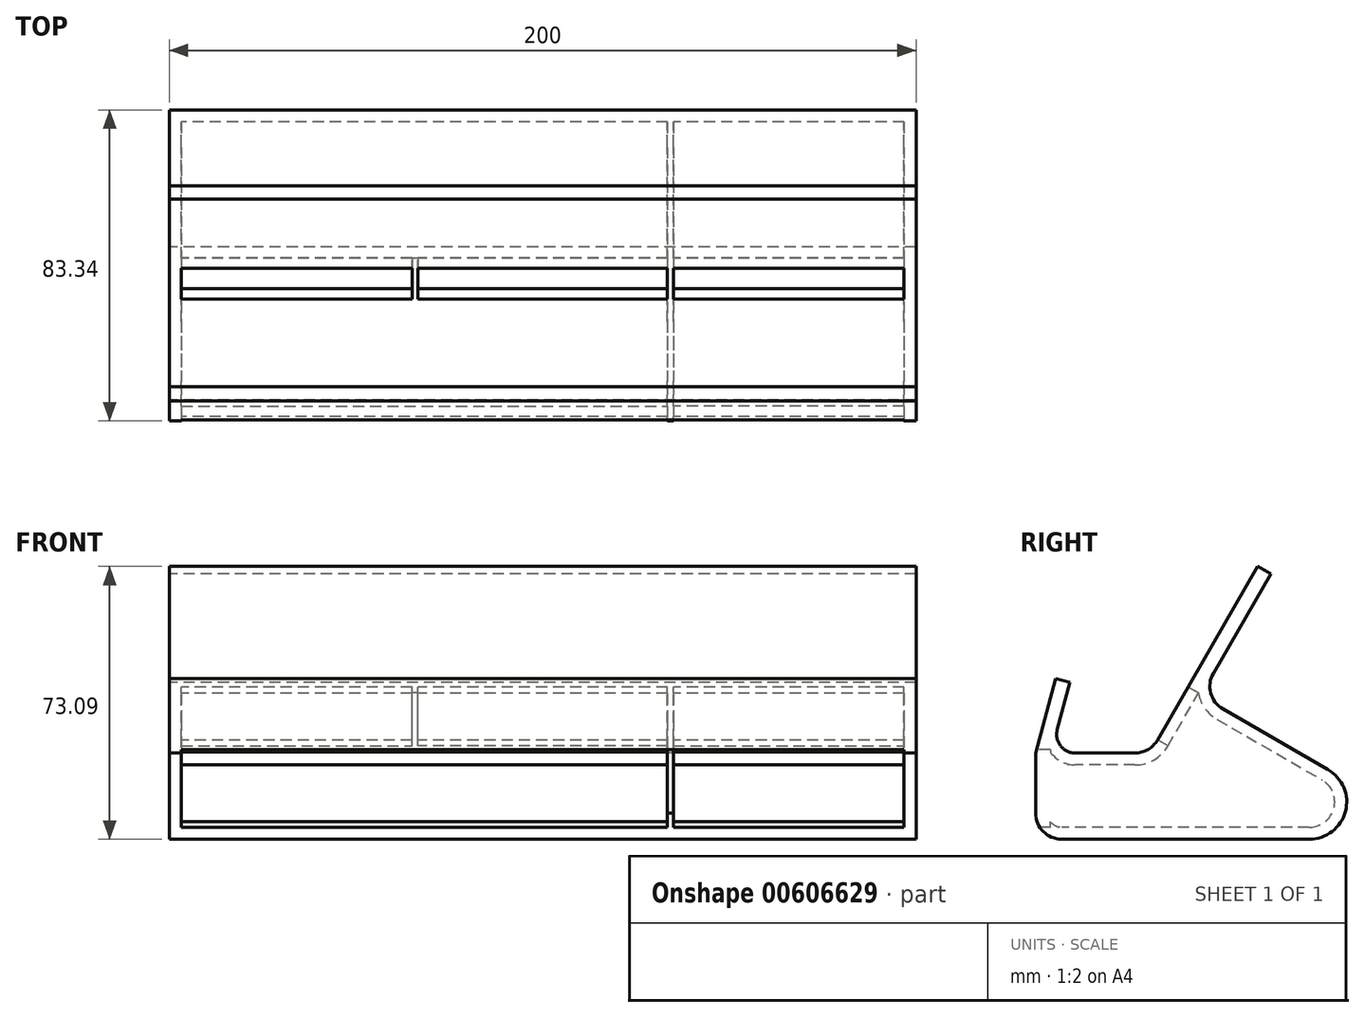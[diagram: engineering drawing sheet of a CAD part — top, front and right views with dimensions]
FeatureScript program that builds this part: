
annotation { "Feature Type Name" : "Feature", "Feature Type Description" : "" }
export const myFeature = defineFeature(function(context is Context, id is Id, definition is map)
    precondition{}
    {
        {
            var Q0;
            Q0=qCreatedBy(makeId("Right.planeOp"),FACE);
            var sketch = newSketch(context, id + "F0", { "sketchPlane" : qUnion([Q0])});
            skLineSegment(sketch, "E0.0", {"start": v(-47.73, -25.37) * mm, "end": v(-44.33, -12.7) * mm});
            skLineSegment(sketch, "E0.1", {"start": v(-22.9, -31.66) * mm, "end": v(-42.9, -31.66) * mm});
            skLineSegment(sketch, "E0.5", {"start": v(-22.9, -31.66) * mm, "end": v(5.97, 18.34) * mm});
            skLineSegment(sketch, "E1.0", {"start": v(-53.56, -31.66) * mm, "end": v(-48.2, -11.66) * mm});
            skLineSegment(sketch, "E2.1", {"start": v(-9.43, -16.34) * mm, "end": v(9.43, 16.34) * mm});
            skLineSegment(sketch, "E3", {"start": v(-48.2, -11.66) * mm, "end": v(-44.33, -12.7) * mm});
            skLineSegment(sketch, "E4", {"start": v(5.97, 18.34) * mm, "end": v(9.43, 16.34) * mm});
            skPoint(sketch, "E5", {"position": v(0, 0) * mm});
            skLineSegment(sketch, "E6", {"start": v(-9.43, -16.34) * mm, "end": v(57.1, -54.75) * mm});
            skLineSegment(sketch, "E7", {"start": v(57.1, -54.75) * mm, "end": v(-53.56, -54.75) * mm});
            skLineSegment(sketch, "E8", {"start": v(-53.56, -54.75) * mm, "end": v(-53.56, -31.66) * mm});
            skLineSegment(sketch, "E9", {"start": v(-9.43, -16.34) * mm, "end": v(-12.9, -14.34) * mm, "construction": true});
            skArc(sketch, "E10", {"start": v(-47.73, -25.37) * mm, "mid": v(-46.86, -29.7) * mm, "end": v(-42.9, -31.66) * mm});
            skSolve(sketch);
        }
        {
            var Q0;
            Q0=qSketchRegion(id+"F0",true);
            extrude(context, id + "F1", {"entities" : qUnion([Q0]), "endBound" : BoundingType.SYMMETRIC, "depth" : 200 * mm, "offsetDistance" : 25 * mm});
        }
        {
            var Q0;
            Q0=makeQuery(id+"F1.opExtrude","SWEPT_EDGE",EDGE,{"disambiguationData":[OSD([sQuery(id+"F0.wireOp",EDGE,"E7"),sQuery(id+"F0.wireOp",EDGE,"E8")])]});
            var Q1;
            Q1=makeQuery(id+"F1.opExtrude","SWEPT_EDGE",EDGE,{"disambiguationData":[OSD([sQuery(id+"F0.wireOp",EDGE,"E2.1"),sQuery(id+"F0.wireOp",EDGE,"E6")])]});
            var Q2;
            Q2=makeQuery(id+"F1.opExtrude","SWEPT_EDGE",EDGE,{"disambiguationData":[OSD([sQuery(id+"F0.wireOp",EDGE,"E0.1"),sQuery(id+"F0.wireOp",EDGE,"E0.5")])]});
            fillet(context, id + "F2", {"entities" : qUnion([Q0, Q1, Q2]), "radius" : 7 * mm, "tangentPropagation" : true, "allowEdgeOverflow" : false});
        }
        {
            var Q0;
            Q0=makeQuery(id+"F1.opExtrude","SWEPT_EDGE",EDGE,{"disambiguationData":[OSD([sQuery(id+"F0.wireOp",EDGE,"E6"),sQuery(id+"F0.wireOp",EDGE,"E7")])]});
            fillet(context, id + "F3", {"entities" : qUnion([Q0]), "radius" : 10 * mm, "tangentPropagation" : true, "allowEdgeOverflow" : false});
        }
        {
            var Q0;
            Q0=makeQuery(id+"F1.opExtrude","SWEPT_FACE",FACE,{"disambiguationData":[OSD([sQuery(id+"F0.wireOp",EDGE,"E8")])]});
            var Q1;
            Q1=makeQuery(id+"F1.opExtrude","SWEPT_BODY",BODY,{"disambiguationData":[OSD([sQuery(id+"F0.wireOp",EDGE,"E0.0"),sQuery(id+"F0.wireOp",EDGE,"E0.1"),sQuery(id+"F0.wireOp",EDGE,"E0.5"),sQuery(id+"F0.wireOp",EDGE,"E1.0"),sQuery(id+"F0.wireOp",EDGE,"E2.1"),sQuery(id+"F0.wireOp",EDGE,"E3"),sQuery(id+"F0.wireOp",EDGE,"E4"),sQuery(id+"F0.wireOp",EDGE,"E6"),sQuery(id+"F0.wireOp",EDGE,"E7"),sQuery(id+"F0.wireOp",EDGE,"E8"),sQuery(id+"F0.wireOp",EDGE,"E10")])]});
            shell(context, id + "F4", {"isHollow" : true, "entities" : qUnion([Q0]), "parts" : qUnion([Q1]), "thickness" : 3.2 * mm});
        }
        {
            var Q0;
            Q0=makeQuery(id+"F1.opExtrude","SWEPT_FACE",FACE,{"disambiguationData":[OSD([sQuery(id+"F0.wireOp",EDGE,"E8")])]});
            var sketch = newSketch(context, id + "F5", { "sketchPlane" : qUnion([Q0])});
            skLineSegment(sketch, "E11.bottom", {"start": v(-96.8, -30.76) * mm, "end": v(96.8, -30.76) * mm});
            skLineSegment(sketch, "E11.left", {"start": v(-96.8, -30.76) * mm, "end": v(-96.8, -51.55) * mm});
            skLineSegment(sketch, "E11.right", {"start": v(96.8, -30.76) * mm, "end": v(96.8, -51.55) * mm});
            skLineSegment(sketch, "E12", {"start": v(96.8, -51.55) * mm, "end": v(-96.8, -51.55) * mm});
            skSolve(sketch);
        }
        {
            var Q0;
            Q0 = qSketchRegion(id + "F5", true);
            extrude(context, id + "F6", {"entities" : qUnion([Q0]), "operationType" : NewBodyOperationType.REMOVE, "oppositeDirection" : true, "depth" : 4 * mm, "offsetDistance" : 25 * mm});
        }
        {
            var Q0;
            Q0=qCreatedBy(makeId("Right.planeOp"),FACE);
            cPlane(context, id + "F7", {"entities" : qUnion([Q0]), "cplaneType" : CPlaneType.OFFSET, "offset" : 35 * mm, "width" : 150 * mm, "height" : 150 * mm});
        }
        {
            var Q0;
            Q0=qCreatedBy(id+"F7.planeOp",FACE);
            var sketch = newSketch(context, id + "F8", { "sketchPlane" : qUnion([Q0])});
            skLineSegment(sketch, "E13.0", {"start": v(-49.56, -30.76) * mm, "end": v(-53.31, -30.76) * mm});
            skLineSegment(sketch, "E14.0", {"start": v(-49.56, -30.76) * mm, "end": v(-49.56, -31.45) * mm});
            skLineSegment(sketch, "E15.0", {"start": v(-49.56, -30.76) * mm, "end": v(-49.56, -30.76) * mm});
            skArc(sketch, "E16.0", {"start": v(-49.56, -31.45) * mm, "mid": v(-46.64, -33.96) * mm, "end": v(-42.9, -34.86) * mm});
            skLineSegment(sketch, "E17.0", {"start": v(-26.94, -34.86) * mm, "end": v(-42.9, -34.86) * mm});
            skLineSegment(sketch, "E18.0", {"start": v(-18.1, -29.76) * mm, "end": v(-9.91, -15.57) * mm});
            skArc(sketch, "E19.0", {"start": v(-18.1, -29.76) * mm, "mid": v(-21.84, -33.5) * mm, "end": v(-26.94, -34.86) * mm});
            skArc(sketch, "E20.0", {"start": v(-4.97, -22.61) * mm, "mid": v(-8.22, -19.64) * mm, "end": v(-9.91, -15.57) * mm});
            skLineSegment(sketch, "E21.0", {"start": v(-4.97, -22.61) * mm, "end": v(23.18, -38.87) * mm});
            skArc(sketch, "E22.0", {"start": v(19.78, -51.55) * mm, "mid": v(26.35, -46.51) * mm, "end": v(23.18, -38.87) * mm});
            skLineSegment(sketch, "E23.0", {"start": v(19.78, -51.55) * mm, "end": v(-46.56, -51.55) * mm});
            skLineSegment(sketch, "E24.0", {"start": v(-46.56, -51.55) * mm, "end": v(-52.43, -51.55) * mm});
            skLineSegment(sketch, "E25.0", {"start": v(-46.56, -51.55) * mm, "end": v(-46.56, -51.55) * mm});
            skLineSegment(sketch, "E26", {"start": v(-53.31, -30.76) * mm, "end": v(-53.56, -47.75) * mm});
            skArc(sketch, "E27", {"start": v(-53.56, -47.75) * mm, "mid": v(-53.27, -49.74) * mm, "end": v(-52.43, -51.55) * mm});
            skSolve(sketch);
        }
        {
            var Q0;
            Q0 = qSketchRegion(id + "F8", true);
            extrude(context, id + "F9", {"entities" : qUnion([Q0]), "operationType" : NewBodyOperationType.ADD, "oppositeDirection" : true, "depth" : 1.6 * mm, "offsetDistance" : 25 * mm});
        }
        {
            var Q0;
            Q0=makeQuery(id+"F1.opExtrude","SWEPT_FACE",FACE,{"disambiguationData":[OSD([sQuery(id+"F0.wireOp",EDGE,"E0.5")])]});
            var sketch = newSketch(context, id + "F10", { "sketchPlane" : qUnion([Q0])});
            skLineSegment(sketch, "E28.bottom", {"start": v(-35, -34.83) * mm, "end": v(-96.8, -34.83) * mm});
            skLineSegment(sketch, "E28.top", {"start": v(-35, -18.44) * mm, "end": v(-96.8, -18.44) * mm});
            skLineSegment(sketch, "E28.left", {"start": v(-35, -34.83) * mm, "end": v(-35, -18.44) * mm});
            skLineSegment(sketch, "E28.right", {"start": v(-96.8, -34.83) * mm, "end": v(-96.8, -18.44) * mm});
            skLineSegment(sketch, "E29.bottom", {"start": v(33.4, -34.83) * mm, "end": v(-33.4, -34.83) * mm});
            skLineSegment(sketch, "E29.top", {"start": v(33.4, -18.44) * mm, "end": v(-33.4, -18.44) * mm});
            skLineSegment(sketch, "E29.left", {"start": v(33.4, -34.83) * mm, "end": v(33.4, -18.44) * mm});
            skLineSegment(sketch, "E29.right", {"start": v(-33.4, -34.83) * mm, "end": v(-33.4, -18.44) * mm});
            skLineSegment(sketch, "E30.bottom", {"start": v(96.8, -34.83) * mm, "end": v(35, -34.83) * mm});
            skLineSegment(sketch, "E30.top", {"start": v(96.8, -18.44) * mm, "end": v(35, -18.44) * mm});
            skLineSegment(sketch, "E30.left", {"start": v(96.8, -34.83) * mm, "end": v(96.8, -18.44) * mm});
            skLineSegment(sketch, "E30.right", {"start": v(35, -34.83) * mm, "end": v(35, -18.44) * mm});
            skSolve(sketch);
        }
        {
            var Q0;
            Q0 = qSketchRegion(id + "F10", true);
            extrude(context, id + "F11", {"entities" : qUnion([Q0]), "operationType" : NewBodyOperationType.REMOVE, "oppositeDirection" : true, "depth" : 3.25 * mm, "offsetDistance" : 25 * mm});
        }
    });
